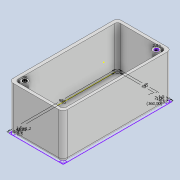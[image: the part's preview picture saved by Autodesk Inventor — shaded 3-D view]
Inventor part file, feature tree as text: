
AUTODESK INVENTOR PART (.ipt)
format: ipt  version: 2020 (Build 240168000, 168)  size: 242,176 bytes
history: native  units: mm
features: extrude x7, sketch x3, fillet x1
ambient origin geometry x8: Origin, YZ Plane, XZ Plane, XY Plane, X Axis, Y Axis, Z Axis, Center Point
bodies: Body1 (feature_tree)
feature tree (11):
  sketch  "Sketch1"  dims[d0=45.0mm d1=90.0mm]
  extrude  "Extrusion3"  Depth=90.0mm
  extrude  "Extrusion4"  Depth=85.0mm
  fillet  "Fillet1"  Radius=2.5mm
  sketch  "Sketch2"  dims[d2=40.0mm d3=85.0mm d8=2.5mm]
  extrude  "Extrusion5"  Depth=2.5mm TaperAngle=0.0deg
  extrude  "Extrusion6"  Depth=37.5mm TaperAngle=0.0deg
  sketch  "Sketch3"  dims[d9=2.5mm d24=2.5mm d25=0.0mm d26=37.5mm d27=0.0mm d28=3.0mm d29=1.5mm d30=1.5mm d31=2.75mm d32=5.5mm d33=1.5mm d34=1.5mm d35=2.75mm d36=45.0deg d37=5.5mm d38=20.0mm d40=360.0deg d43=20.0mm d44=1.2mm d45=1.2mm d46=35.0mm d47=0.0mm d48=10.0mm d49=0.0mm d50=3.0mm d51=2.5mm d52=3.0mm d53=2.5mm d54=0.5mm d55=0.0mm d56=20.0mm d57=0.0mm d58=32.0mm d59=0.0mm d60=0.5mm d61=0.872665mm]
  extrude  "Extrusion7"  Depth=3.0mm
  extrude  "Extrusion8"  Depth=1.5mm
  extrude  "Extrusion9"  Depth=1.5mm
